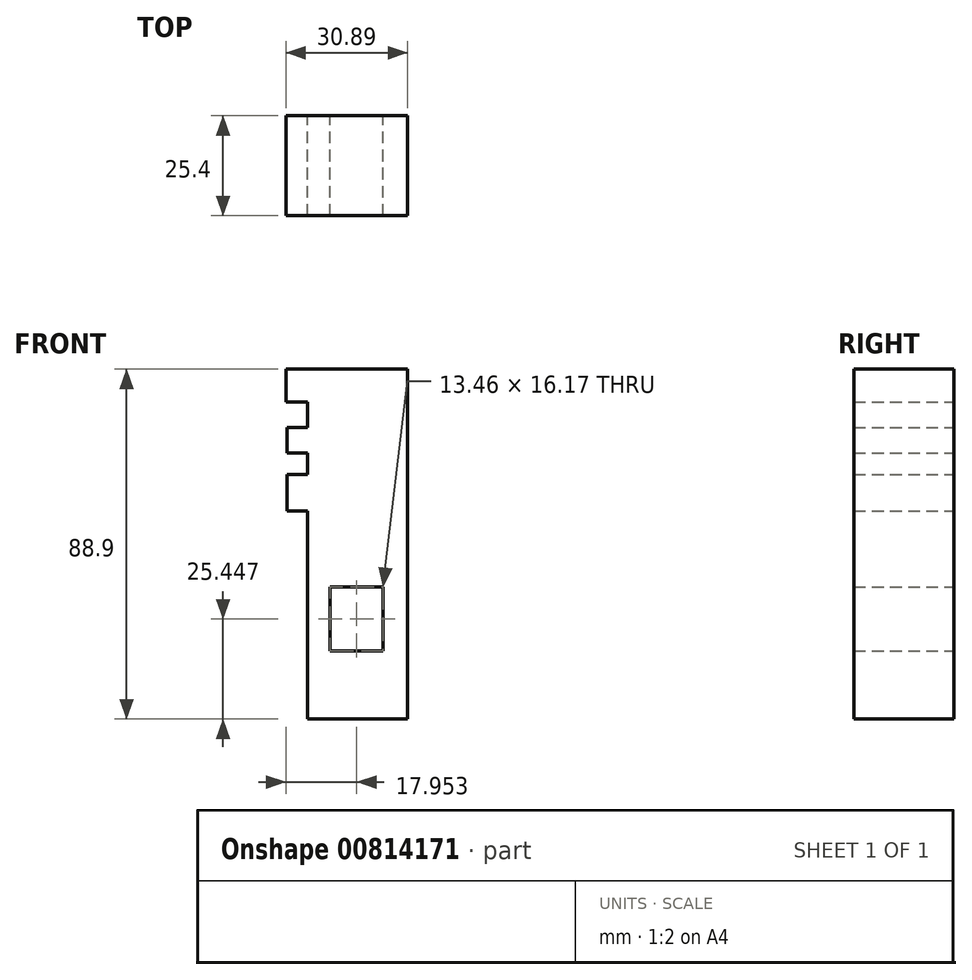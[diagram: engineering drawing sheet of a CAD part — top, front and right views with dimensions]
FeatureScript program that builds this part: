
annotation { "Feature Type Name" : "Feature", "Feature Type Description" : "" }
export const myFeature = defineFeature(function(context is Context, id is Id, definition is map)
    precondition{}
    {
        {
            var Q0;
            Q0=qCreatedBy(makeId("Front.planeOp"),FACE);
            var sketch = newSketch(context, id + "F0", { "sketchPlane" : qUnion([Q0])});
            skLineSegment(sketch, "E0.bottom", {"start": v(-54.5, 21.29) * mm, "end": v(-29.1, 21.29) * mm});
            skLineSegment(sketch, "E0.top", {"start": v(-54.5, -67.61) * mm, "end": v(-29.1, -67.61) * mm});
            skLineSegment(sketch, "E0.left", {"start": v(-54.5, 21.29) * mm, "end": v(-54.5, -67.61) * mm});
            skLineSegment(sketch, "E0.right", {"start": v(-29.1, 21.29) * mm, "end": v(-29.1, -67.61) * mm});
            skLineSegment(sketch, "E1", {"start": v(-54.5, 21.29) * mm, "end": v(-59.99, 21.29) * mm});
            skLineSegment(sketch, "E2", {"start": v(-59.99, 21.29) * mm, "end": v(-59.99, 13) * mm});
            skLineSegment(sketch, "E3", {"start": v(-59.99, 13) * mm, "end": v(-54.5, 13) * mm});
            skLineSegment(sketch, "E4", {"start": v(-54.5, 13) * mm, "end": v(-54.5, 0) * mm});
            skLineSegment(sketch, "E5", {"start": v(-54.5, -16.81) * mm, "end": v(-54.5, -23.16) * mm});
            skLineSegment(sketch, "E6", {"start": v(-54.5, -16.81) * mm, "end": v(-29.1, -16.81) * mm});
            skLineSegment(sketch, "E7", {"start": v(-54.5, 6.5) * mm, "end": v(-59.78, 6.5) * mm});
            skLineSegment(sketch, "E8", {"start": v(-59.78, 6.5) * mm, "end": v(-59.78, 0) * mm});
            skLineSegment(sketch, "E9", {"start": v(-59.78, 0) * mm, "end": v(-54.5, 0) * mm});
            skLineSegment(sketch, "E10", {"start": v(-54.5, -5.44) * mm, "end": v(-59.78, -5.44) * mm});
            skLineSegment(sketch, "E11", {"start": v(-59.78, -5.44) * mm, "end": v(-59.78, -14.68) * mm});
            skLineSegment(sketch, "E12", {"start": v(-59.78, -14.68) * mm, "end": v(-54.5, -14.68) * mm});
            skLineSegment(sketch, "E13.bottom", {"start": v(-48.77, -34.08) * mm, "end": v(-35.3, -34.08) * mm});
            skLineSegment(sketch, "E13.top", {"start": v(-48.77, -50.25) * mm, "end": v(-35.3, -50.25) * mm});
            skLineSegment(sketch, "E13.left", {"start": v(-48.77, -34.08) * mm, "end": v(-48.77, -50.25) * mm});
            skLineSegment(sketch, "E13.right", {"start": v(-35.3, -34.08) * mm, "end": v(-35.3, -50.25) * mm});
            skSolve(sketch);
        }
        {
            var Q0;
            {var subQ2=sQuery(id+"F0.wireOp",EDGE,"E0.top");Q0=makeQuery(id+"F0.imprint","IMPRINT",FACE,{"disambiguationData":[TD([[makeQuery(id+"F0.imprint","IMPRINT",EDGE,{"derivedFrom":subQ2}),1.0]])]});}
            var Q1;
            {var subQ6=sQuery(id+"F0.wireOp",EDGE,"E0.bottom");Q1=makeQuery(id+"F0.imprint","IMPRINT",FACE,{"disambiguationData":[TD([[makeQuery(id+"F0.imprint","IMPRINT",EDGE,{"derivedFrom":subQ6}),-1.0]])]});}
            var Q2;
            {var subQ0=sQuery(id+"F0.wireOp",EDGE,"E1");Q2=makeQuery(id+"F0.imprint","IMPRINT",FACE,{"disambiguationData":[TD([[makeQuery(id+"F0.imprint","IMPRINT",EDGE,{"derivedFrom":subQ0}),1.0]])]});}
            var Q3;
            {var subQ2=sQuery(id+"F0.wireOp",EDGE,"E7");Q3=makeQuery(id+"F0.imprint","IMPRINT",FACE,{"disambiguationData":[TD([[makeQuery(id+"F0.imprint","IMPRINT",EDGE,{"derivedFrom":subQ2}),1.0]])]});}
            var Q4;
            {var subQ0=sQuery(id+"F0.wireOp",EDGE,"E10");Q4=makeQuery(id+"F0.imprint","IMPRINT",FACE,{"disambiguationData":[TD([[makeQuery(id+"F0.imprint","IMPRINT",EDGE,{"derivedFrom":subQ0}),1.0]])]});}
            extrude(context, id + "F1", {"entities" : qUnion([Q0, Q1, Q2, Q3, Q4]), "depth" : 25.4 * mm, "offsetDistance" : 25.4 * mm});
        }
    });
